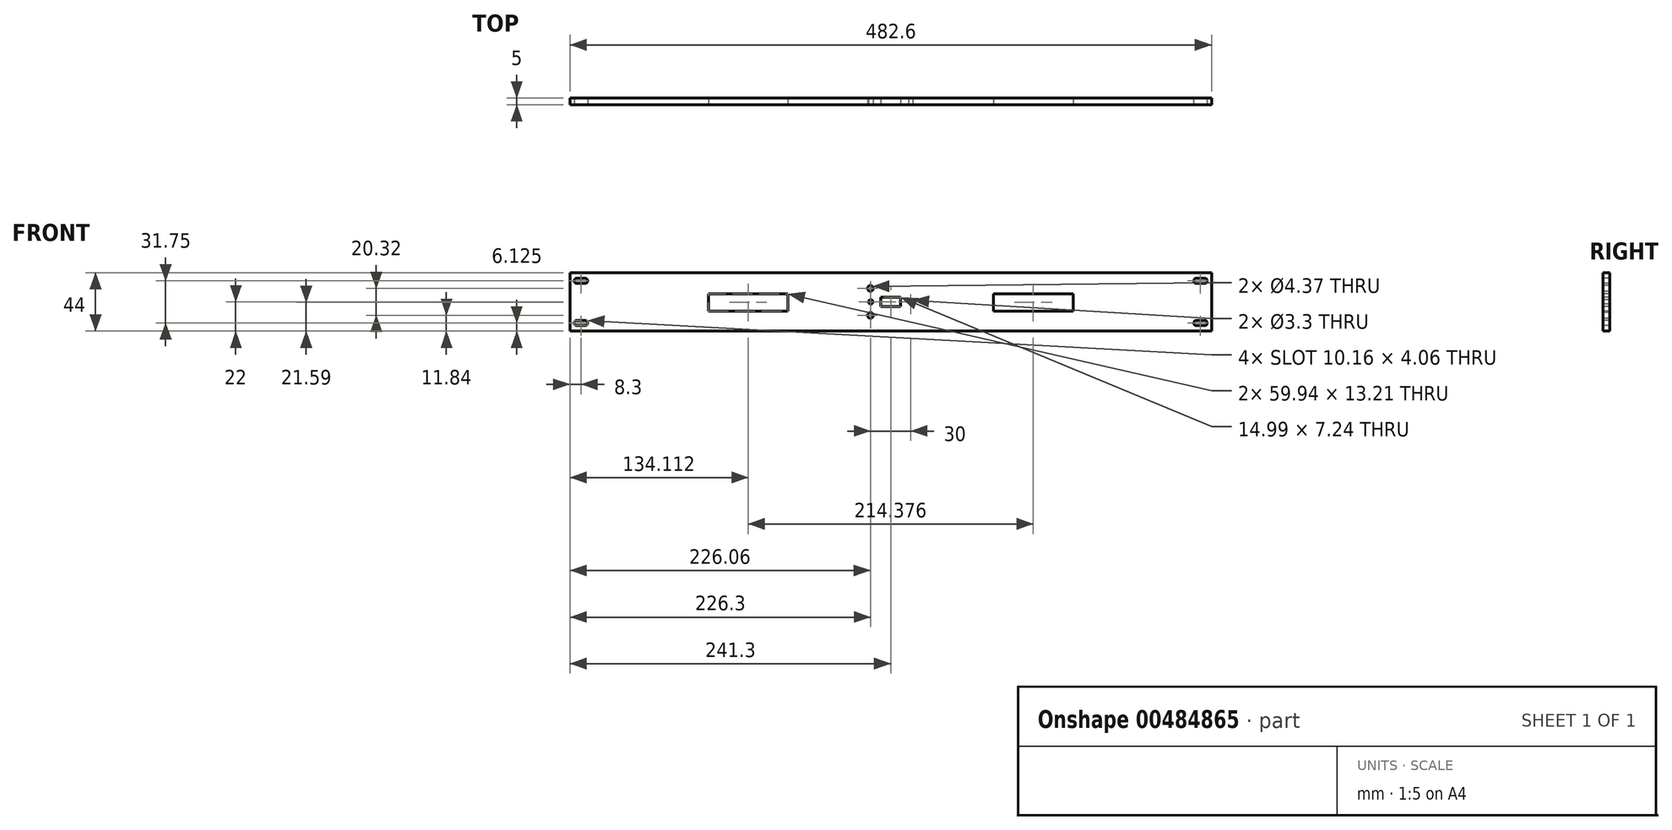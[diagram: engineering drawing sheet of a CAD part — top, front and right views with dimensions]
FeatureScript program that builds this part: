
annotation { "Feature Type Name" : "Feature", "Feature Type Description" : "" }
export const myFeature = defineFeature(function(context is Context, id is Id, definition is map)
    precondition{}
    {
        {
            var Q0;
            Q0=qCreatedBy(makeId("Front.planeOp"),FACE);
            var sketch = newSketch(context, id + "F0", { "sketchPlane" : qUnion([Q0])});
            skLineSegment(sketch, "E0.bottom", {"start": v(0, 0) * mm, "end": v(482.6, 0) * mm});
            skLineSegment(sketch, "E0.top", {"start": v(0, 44) * mm, "end": v(482.6, 44) * mm});
            skLineSegment(sketch, "E0.left", {"start": v(0, 0) * mm, "end": v(0, 44) * mm});
            skLineSegment(sketch, "E0.right", {"start": v(482.6, 0) * mm, "end": v(482.6, 44) * mm});
            skPoint(sketch, "E1", {"position": v(241.3, 44) * mm});
            skPoint(sketch, "E2", {"position": v(241.3, 0) * mm});
            skLineSegment(sketch, "E3", {"start": v(241.3, 44) * mm, "end": v(241.3, 0) * mm, "construction": true});
            skLineSegment(sketch, "E4", {"start": v(0, 22) * mm, "end": v(482.6, 22) * mm, "construction": true});
            skCircle(sketch, "E5", {"center": v(226.06, 11.84) * mm, "radius": 2.18 * mm});
            skLineSegment(sketch, "E6", {"start": v(5.25, 39.9) * mm, "end": v(11.35, 39.9) * mm});
            skLineSegment(sketch, "E7", {"start": v(5.25, 35.84) * mm, "end": v(11.35, 35.84) * mm});
            skArc(sketch, "E8", {"start": v(5.25, 39.9) * mm, "mid": v(3.22, 37.88) * mm, "end": v(5.25, 35.84) * mm});
            skArc(sketch, "E9", {"start": v(11.35, 39.9) * mm, "mid": v(13.38, 37.88) * mm, "end": v(11.35, 35.84) * mm});
            skLineSegment(sketch, "E10", {"start": v(5.25, 37.88) * mm, "end": v(11.35, 37.88) * mm, "construction": true});
            skPoint(sketch, "E11", {"position": v(8.3, 37.88) * mm});
            skLineSegment(sketch, "E12.MirrorCS", {"start": v(5.25, 4.1) * mm, "end": v(11.35, 4.1) * mm});
            skArc(sketch, "E13.MirrorCS", {"start": v(5.25, 4.1) * mm, "mid": v(3.22, 6.12) * mm, "end": v(5.25, 8.16) * mm});
            skLineSegment(sketch, "E14.MirrorCS", {"start": v(5.25, 8.16) * mm, "end": v(11.35, 8.16) * mm});
            skArc(sketch, "E15.MirrorCS", {"start": v(11.35, 4.1) * mm, "mid": v(13.38, 6.12) * mm, "end": v(11.35, 8.16) * mm});
            skLineSegment(sketch, "E16.MirrorCS", {"start": v(5.25, 6.12) * mm, "end": v(11.35, 6.12) * mm, "construction": true});
            skLineSegment(sketch, "E17.MirrorCS", {"start": v(477.35, 39.9) * mm, "end": v(471.25, 39.9) * mm});
            skArc(sketch, "E18.MirrorCS", {"start": v(471.25, 39.9) * mm, "mid": v(469.22, 37.88) * mm, "end": v(471.25, 35.84) * mm});
            skLineSegment(sketch, "E19.MirrorCS", {"start": v(477.35, 35.84) * mm, "end": v(471.25, 35.84) * mm});
            skArc(sketch, "E20.MirrorCS", {"start": v(477.35, 39.9) * mm, "mid": v(479.38, 37.88) * mm, "end": v(477.35, 35.84) * mm});
            skLineSegment(sketch, "E21.MirrorCS", {"start": v(477.35, 8.16) * mm, "end": v(471.25, 8.16) * mm});
            skArc(sketch, "E22.MirrorCS", {"start": v(471.25, 4.1) * mm, "mid": v(469.22, 6.12) * mm, "end": v(471.25, 8.16) * mm});
            skLineSegment(sketch, "E23.MirrorCS", {"start": v(477.35, 4.1) * mm, "end": v(471.25, 4.1) * mm});
            skArc(sketch, "E24.MirrorCS", {"start": v(477.35, 4.1) * mm, "mid": v(479.38, 6.12) * mm, "end": v(477.35, 8.16) * mm});
            skLineSegment(sketch, "E25.MirrorCS", {"start": v(477.35, 6.12) * mm, "end": v(471.25, 6.12) * mm, "construction": true});
            skLineSegment(sketch, "E26.MirrorCS", {"start": v(477.35, 37.88) * mm, "end": v(471.25, 37.88) * mm, "construction": true});
            skLineSegment(sketch, "E27", {"start": v(30.16, 44) * mm, "end": v(30.16, 0) * mm, "construction": true});
            skLineSegment(sketch, "E28.MirrorCS", {"start": v(452.44, 44) * mm, "end": v(452.44, 0) * mm, "construction": true});
            skLineSegment(sketch, "E29", {"start": v(0, 5.5) * mm, "end": v(482.6, 5.5) * mm, "construction": true});
            skLineSegment(sketch, "E30.bottom", {"start": v(233.8, 25.62) * mm, "end": v(248.8, 25.62) * mm});
            skLineSegment(sketch, "E30.top", {"start": v(233.8, 18.38) * mm, "end": v(248.8, 18.38) * mm});
            skLineSegment(sketch, "E30.left", {"start": v(233.8, 25.62) * mm, "end": v(233.8, 18.38) * mm});
            skLineSegment(sketch, "E30.right", {"start": v(248.8, 25.62) * mm, "end": v(248.8, 18.38) * mm});
            skPoint(sketch, "E30.middle", {"position": v(241.3, 22) * mm});
            skCircle(sketch, "E31.MirrorC", {"center": v(226.3, 22) * mm, "radius": 1.65 * mm});
            skCircle(sketch, "E32.MirrorC", {"center": v(226.06, 32.16) * mm, "radius": 2.18 * mm});
            skLineSegment(sketch, "E33", {"start": v(0, 38.5) * mm, "end": v(482.6, 38.5) * mm, "construction": true});
            skCircle(sketch, "E34.MirrorC", {"center": v(256.3, 22) * mm, "radius": 1.65 * mm});
            skSolve(sketch);
        }
        {
            var Q0;
            {var subQ0=sQuery(id+"F0.wireOp",EDGE,"E0.right");Q0=makeQuery(id+"F0.imprint","IMPRINT",FACE,{"disambiguationData":[TD([[makeQuery(id+"F0.imprint","IMPRINT",EDGE,{"derivedFrom":subQ0}),1.0]])]});}
            extrude(context, id + "F1", {"entities" : qUnion([Q0]), "oppositeDirection" : true, "depth" : 5 * mm});
        }
        {
            var Q0;
            Q0=makeQuery(id+"F0.imprint","IMPRINT",FACE,{"disambiguationData":[TD([[makeQuery(id+"F0.imprint","IMPRINT",EDGE,{"derivedFrom":sQuery(id+"F0.wireOp",EDGE,"E0.bottom")}),1.0]])]});
            var sketch = newSketch(context, id + "F2", { "sketchPlane" : qUnion([Q0])});
            skLineSegment(sketch, "E35.bottom", {"start": v(104.14, 28.2) * mm, "end": v(164.08, 28.2) * mm});
            skLineSegment(sketch, "E35.top", {"start": v(104.14, 14.99) * mm, "end": v(164.08, 14.99) * mm});
            skLineSegment(sketch, "E35.left", {"start": v(104.14, 28.2) * mm, "end": v(104.14, 14.99) * mm});
            skLineSegment(sketch, "E35.right", {"start": v(164.08, 28.2) * mm, "end": v(164.08, 14.99) * mm});
            skPoint(sketch, "E36", {"position": v(67.43, 22) * mm});
            skPoint(sketch, "E37", {"position": v(197.64, 22) * mm});
            skLineSegment(sketch, "E38.bottom", {"start": v(318.52, 28.2) * mm, "end": v(378.46, 28.2) * mm});
            skLineSegment(sketch, "E38.top", {"start": v(318.52, 14.99) * mm, "end": v(378.46, 14.99) * mm});
            skLineSegment(sketch, "E38.left", {"start": v(318.52, 28.2) * mm, "end": v(318.52, 14.99) * mm});
            skLineSegment(sketch, "E38.right", {"start": v(378.46, 28.2) * mm, "end": v(378.46, 14.99) * mm});
            skPoint(sketch, "E39", {"position": v(281.8, 22) * mm});
            skPoint(sketch, "E40", {"position": v(412.01, 22) * mm});
            skSolve(sketch);
        }
        {
            var Q0;
            Q0=makeQuery(id+"F2.imprint","IMPRINT",FACE,{"disambiguationData":[TD([[makeQuery(id+"F2.imprint","IMPRINT",EDGE,{"derivedFrom":sQuery(id+"F2.wireOp",EDGE,"E35.bottom")}),-1.0]])]});
            var Q1;
            Q1=makeQuery(id+"F2.imprint","IMPRINT",FACE,{"disambiguationData":[TD([[makeQuery(id+"F2.imprint","IMPRINT",EDGE,{"derivedFrom":sQuery(id+"F2.wireOp",EDGE,"E38.bottom")}),-1.0]])]});
            extrude(context, id + "F3", {"entities" : qUnion([Q0, Q1]), "operationType" : NewBodyOperationType.REMOVE, "endBound" : BoundingType.THROUGH_ALL, "oppositeDirection" : true, "depth" : 25.4 * mm});
        }
    });
